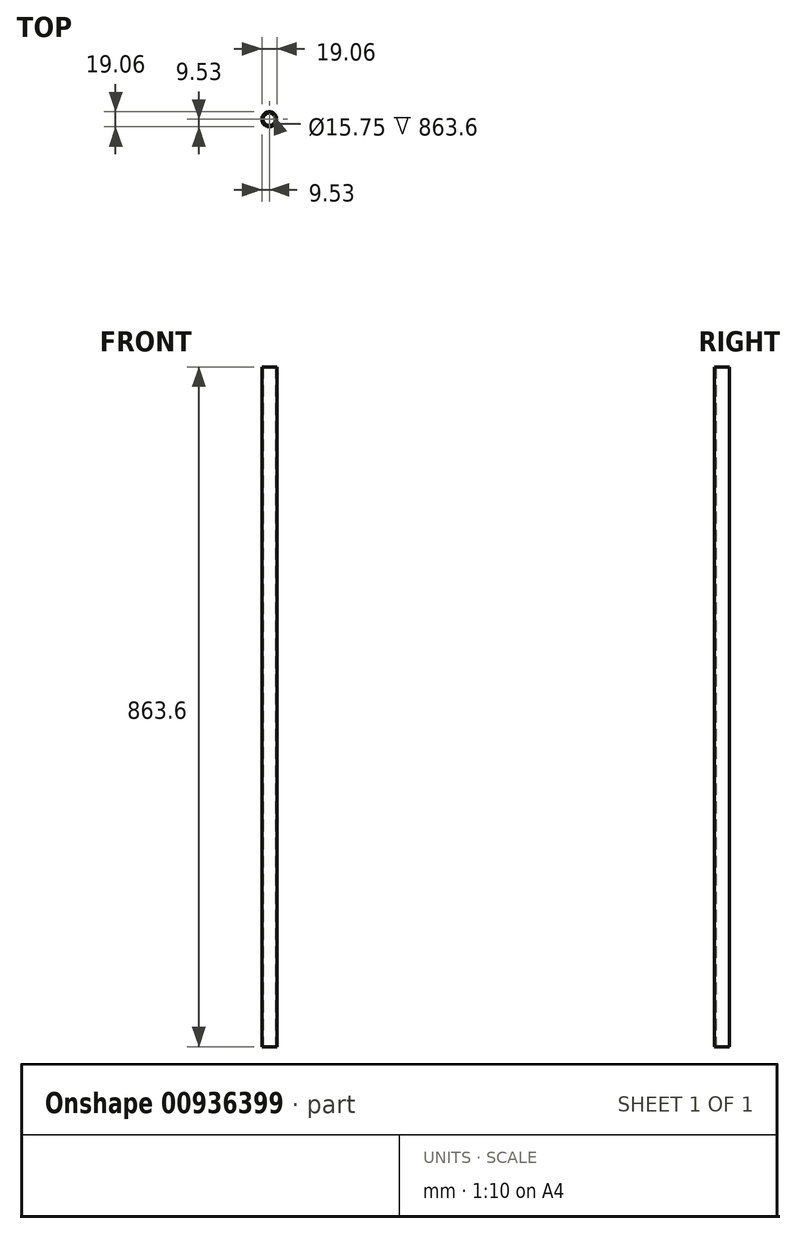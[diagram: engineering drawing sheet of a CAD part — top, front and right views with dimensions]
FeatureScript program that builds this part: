
annotation { "Feature Type Name" : "Feature", "Feature Type Description" : "" }
export const myFeature = defineFeature(function(context is Context, id is Id, definition is map)
    precondition{}
    {
        {
            var Q0;
            Q0=qCreatedBy(makeId("Top.planeOp"),FACE);
            var sketch = newSketch(context, id + "F0", { "sketchPlane" : qUnion([Q0])});
            skCircle(sketch, "E0", {"center": v(0, 0) * mm, "radius": 9.53 * mm});
            skCircle(sketch, "E1", {"center": v(0, 0) * mm, "radius": 7.87 * mm});
            skSolve(sketch);
        }
        {
            var Q0;
            Q0=makeQuery(id+"F0.imprint","IMPRINT",FACE,{"disambiguationData":[TD([[makeQuery(id+"F0.imprint","IMPRINT",EDGE,{"derivedFrom":sQuery(id+"F0.wireOp",EDGE,"E0")}),1.0]])]});
            extrude(context, id + "F1", {"entities" : qUnion([Q0]), "depth" : 863.6 * mm, "offsetDistance" : 25.4 * mm});
        }
    });
